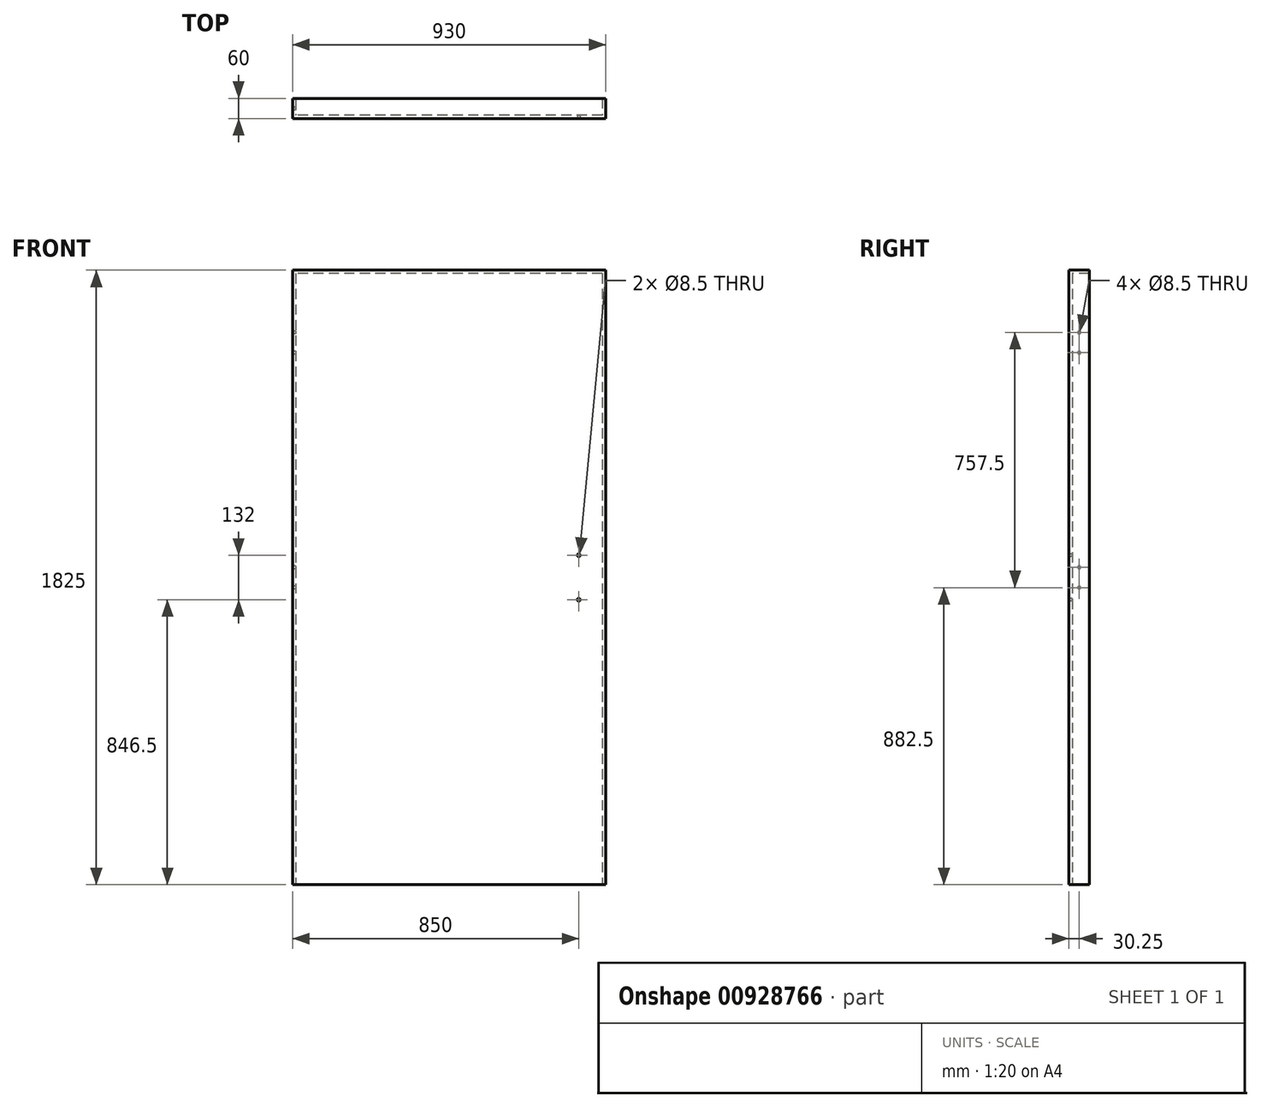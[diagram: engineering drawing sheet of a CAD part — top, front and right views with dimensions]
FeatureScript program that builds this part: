
annotation { "Feature Type Name" : "Feature", "Feature Type Description" : "" }
export const myFeature = defineFeature(function(context is Context, id is Id, definition is map)
    precondition{}
    {
        {
            var Q0;
            Q0=qCreatedBy(makeId("Front.planeOp"),FACE);
            var sketch = newSketch(context, id + "F0", { "sketchPlane" : qUnion([Q0])});
            skLineSegment(sketch, "E0.bottom", {"start": v(465, 912.5) * mm, "end": v(-465, 912.5) * mm});
            skLineSegment(sketch, "E0.top", {"start": v(465, -912.5) * mm, "end": v(-465, -912.5) * mm});
            skLineSegment(sketch, "E0.left", {"start": v(465, 912.5) * mm, "end": v(465, -912.5) * mm});
            skLineSegment(sketch, "E0.right", {"start": v(-465, 912.5) * mm, "end": v(-465, -912.5) * mm});
            skPoint(sketch, "E0.middle", {"position": v(0, 0) * mm});
            skSolve(sketch);
        }
        {
            var Q0;
            Q0=makeQuery(id+"F0.imprint","IMPRINT",FACE,{"disambiguationData":[TD([[makeQuery(id+"F0.imprint","IMPRINT",EDGE,{"derivedFrom":sQuery(id+"F0.wireOp",EDGE,"E0.bottom")}),1.0]])]});
            extrude(context, id + "F1", {"entities" : qUnion([Q0]), "depth" : 10 * mm, "offsetDistance" : 25 * mm});
        }
        {
            var Q0;
            Q0=makeQuery(id+"F1.opExtrude","CAP_FACE",FACE,{"disambiguationData":[OSD([sQuery(id+"F0.wireOp",EDGE,"E0.bottom"),sQuery(id+"F0.wireOp",EDGE,"E0.top"),sQuery(id+"F0.wireOp",EDGE,"E0.left"),sQuery(id+"F0.wireOp",EDGE,"E0.right")])],"isStart":true});
            var sketch = newSketch(context, id + "F2", { "sketchPlane" : qUnion([Q0])});
            skLineSegment(sketch, "E1.0", {"start": v(-465, 912.5) * mm, "end": v(465, 912.5) * mm});
            skLineSegment(sketch, "E2.0", {"start": v(465, 912.5) * mm, "end": v(465, -912.5) * mm});
            skLineSegment(sketch, "E3.0", {"start": v(455, 902.5) * mm, "end": v(455, -912.5) * mm});
            skLineSegment(sketch, "E3.1", {"start": v(-455, 902.5) * mm, "end": v(455, 902.5) * mm});
            skLineSegment(sketch, "E4", {"start": v(-465, 912.5) * mm, "end": v(-465, -912.5) * mm});
            skLineSegment(sketch, "E5.0", {"start": v(-455, 902.5) * mm, "end": v(-455, -912.5) * mm});
            skLineSegment(sketch, "E6", {"start": v(455, -912.5) * mm, "end": v(465, -912.5) * mm});
            skLineSegment(sketch, "E7", {"start": v(-455, -912.5) * mm, "end": v(-465, -912.5) * mm});
            skSolve(sketch);
        }
        {
            var Q0;
            {var subQ3=sQuery(id+"F2.wireOp",EDGE,"E1.0");Q0=makeQuery(id+"F2.imprint","IMPRINT",FACE,{"disambiguationData":[TD([[makeQuery(id+"F2.imprint","IMPRINT",EDGE,{"derivedFrom":subQ3}),-1.0]])]});}
            extrude(context, id + "F3", {"entities" : qUnion([Q0]), "operationType" : NewBodyOperationType.ADD, "depth" : 50 * mm, "offsetDistance" : 25 * mm});
        }
        {
            var Q0;
            Q0=makeQuery(id+"F1.opExtrude","CAP_FACE",FACE,{"disambiguationData":[OSD([sQuery(id+"F0.wireOp",EDGE,"E0.bottom"),sQuery(id+"F0.wireOp",EDGE,"E0.top"),sQuery(id+"F0.wireOp",EDGE,"E0.left"),sQuery(id+"F0.wireOp",EDGE,"E0.right")])],"isStart":false});
            var sketch = newSketch(context, id + "F4", { "sketchPlane" : qUnion([Q0])});
            skLineSegment(sketch, "E8", {"start": v(0, 0) * mm, "end": v(385, 0) * mm});
            skLineSegment(sketch, "E9", {"start": v(385, 66) * mm, "end": v(385, -66) * mm});
            skPoint(sketch, "E10", {"position": v(385, 66) * mm});
            skPoint(sketch, "E11", {"position": v(385, -66) * mm});
            skSolve(sketch);
        }
        {
            var Q0;
            Q0=sQuery(id+"F4.wireOp",VERTEX,"E10");
            var Q1;
            Q1=sQuery(id+"F4.wireOp",VERTEX,"E11");
            var Q2;
            Q2=makeQuery(id+"F1.opExtrude","SWEPT_BODY",BODY,{"disambiguationData":[OSD([sQuery(id+"F0.wireOp",EDGE,"E0.bottom"),sQuery(id+"F0.wireOp",EDGE,"E0.top"),sQuery(id+"F0.wireOp",EDGE,"E0.left"),sQuery(id+"F0.wireOp",EDGE,"E0.right")])]});
            hole(context, id + "F5", {"style" : HoleStyle.SIMPLE, "endStyle" : HoleEndStyle.THROUGH, "holeDiameter" : 8.5 * mm, "majorDiameter" : 5 * mm, "isTappedThrough" : true, "tappedDepth" : 12 * mm, "tapClearance" : 3, "locations" : qUnion([Q0, Q1]), "scope" : qUnion([Q2])});
        }
        {
            var Q0;
            Q0=makeQuery(id+"F3.boolean.opBoolean","MERGE",FACE,{"derivedFrom":[makeQuery(id+"F1.opExtrude","SWEPT_FACE",FACE,{"disambiguationData":[OSD([sQuery(id+"F0.wireOp",EDGE,"E0.right")])]}),makeQuery(id+"F3.opExtrude","SWEPT_FACE",FACE,{"disambiguationData":[OSD([sQuery(id+"F2.wireOp",EDGE,"E2.0")])]})]});
            var sketch = newSketch(context, id + "F6", { "sketchPlane" : qUnion([Q0])});
            skPoint(sketch, "E12", {"position": v(-20.25, 727.5) * mm});
            skPoint(sketch, "E13", {"position": v(-20.25, 667.5) * mm});
            skPoint(sketch, "E14", {"position": v(-20.25, 1157.5) * mm});
            skPoint(sketch, "E15", {"position": v(-20.25, 1097.5) * mm});
            skPoint(sketch, "E16", {"position": v(-20.25, 30) * mm});
            skPoint(sketch, "E17", {"position": v(-20.25, -30) * mm});
            skLineSegment(sketch, "E18", {"start": v(-20.25, 30) * mm, "end": v(-20.25, -30) * mm});
            skLineSegment(sketch, "E19", {"start": v(-20.25, 0) * mm, "end": v(0, 0) * mm});
            skSolve(sketch);
        }
        {
            var Q0;
            Q0=sQuery(id+"F6.wireOp",VERTEX,"E12");
            var Q1;
            Q1=sQuery(id+"F6.wireOp",VERTEX,"E13");
            var Q2;
            Q2=sQuery(id+"F6.wireOp",VERTEX,"E14");
            var Q3;
            Q3=sQuery(id+"F6.wireOp",VERTEX,"E15");
            var Q4;
            Q4=sQuery(id+"F6.wireOp",VERTEX,"E16");
            var Q5;
            Q5=sQuery(id+"F6.wireOp",VERTEX,"E17");
            var Q6;
            Q6=makeQuery(id+"F1.opExtrude","SWEPT_BODY",BODY,{"disambiguationData":[OSD([sQuery(id+"F0.wireOp",EDGE,"E0.bottom"),sQuery(id+"F0.wireOp",EDGE,"E0.top"),sQuery(id+"F0.wireOp",EDGE,"E0.left"),sQuery(id+"F0.wireOp",EDGE,"E0.right")])]});
            hole(context, id + "F7", {"style" : HoleStyle.SIMPLE, "endStyle" : HoleEndStyle.BLIND, "holeDiameter" : 8.5 * mm, "majorDiameter" : 5 * mm, "holeDepth" : 15 * mm, "isTappedThrough" : true, "tappedDepth" : 12 * mm, "tapClearance" : 3, "locations" : qUnion([Q0, Q1, Q2, Q3, Q4, Q5]), "scope" : qUnion([Q6])});
        }
    });
